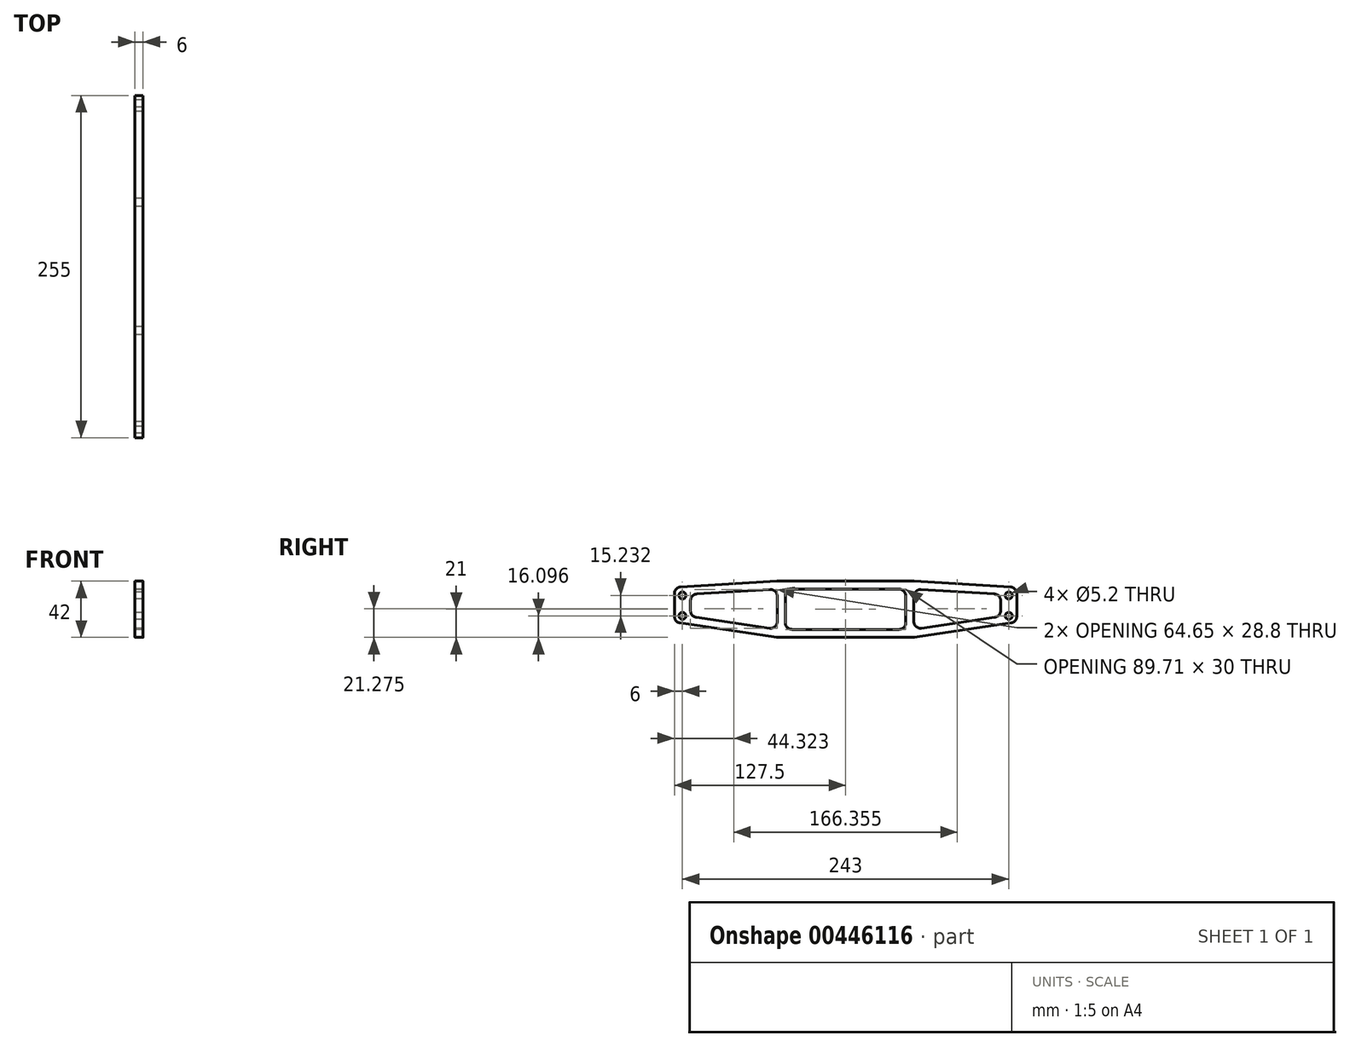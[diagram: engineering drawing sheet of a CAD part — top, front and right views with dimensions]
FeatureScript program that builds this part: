
annotation { "Feature Type Name" : "Feature", "Feature Type Description" : "" }
export const myFeature = defineFeature(function(context is Context, id is Id, definition is map)
    precondition{}
    {
        {
            var Q0;
            Q0=qCreatedBy(makeId("Right.planeOp"),FACE);
            var sketch = newSketch(context, id + "F0", { "sketchPlane" : qUnion([Q0])});
            skLineSegment(sketch, "E0.bottom", {"start": v(0, 0) * mm, "end": v(-50.48, 0) * mm});
            skLineSegment(sketch, "E0.top", {"start": v(39.16, 42) * mm, "end": v(-50.7, 42) * mm});
            skLineSegment(sketch, "E0.right", {"start": v(-50.86, 11.87) * mm, "end": v(-50.86, 30.68) * mm});
            skLineSegment(sketch, "E1", {"start": v(-127.5, 15.73) * mm, "end": v(-127.5, 32.7) * mm});
            skLineSegment(sketch, "E2", {"start": v(-122.8, 37.7) * mm, "end": v(-51, 42) * mm});
            skLineSegment(sketch, "E3", {"start": v(-123.24, 10.78) * mm, "end": v(-51.22, 0.05) * mm});
            skLineSegment(sketch, "E4.0", {"start": v(-110.8, 32.4) * mm, "end": v(-56.15, 35.67) * mm});
            skLineSegment(sketch, "E5.0", {"start": v(-111.24, 15.06) * mm, "end": v(-56.6, 6.92) * mm});
            skLineSegment(sketch, "E6.0", {"start": v(-44.86, 11) * mm, "end": v(-44.86, 31) * mm});
            skLineSegment(sketch, "E7.0", {"start": v(39.16, 36) * mm, "end": v(-39.86, 36) * mm});
            skLineSegment(sketch, "E8.0", {"start": v(0, 6) * mm, "end": v(-39.86, 6) * mm});
            skLineSegment(sketch, "E9.0", {"start": v(-115.5, 20) * mm, "end": v(-115.5, 27.42) * mm});
            skPoint(sketch, "E10.visualSharp", {"position": v(-127.5, 37.42) * mm});
            skArc(sketch, "E10.filletArc", {"start": v(-122.8, 37.7) * mm, "mid": v(-126.14, 36.14) * mm, "end": v(-127.5, 32.7) * mm});
            skPoint(sketch, "E11.visualSharp", {"position": v(-127.5, 11.42) * mm});
            skArc(sketch, "E11.filletArc", {"start": v(-127.5, 15.73) * mm, "mid": v(-126.29, 12.47) * mm, "end": v(-123.24, 10.78) * mm});
            skPoint(sketch, "E12.visualSharp", {"position": v(-115.5, 15.7) * mm});
            skArc(sketch, "E12.filletArc", {"start": v(-115.5, 20) * mm, "mid": v(-114.29, 16.74) * mm, "end": v(-111.24, 15.06) * mm});
            skPoint(sketch, "E13.visualSharp", {"position": v(-115.5, 32.13) * mm});
            skArc(sketch, "E13.filletArc", {"start": v(-110.8, 32.4) * mm, "mid": v(-114.14, 30.84) * mm, "end": v(-115.5, 27.42) * mm});
            skPoint(sketch, "E14.visualSharp", {"position": v(-50.86, 0) * mm});
            skArc(sketch, "E14.filletArc", {"start": v(-51.22, 0.05) * mm, "mid": v(-50.85, 0.01) * mm, "end": v(-50.48, 0) * mm});
            skPoint(sketch, "E15.visualSharp", {"position": v(-50.86, 42) * mm});
            skArc(sketch, "E15.filletArc", {"start": v(-50.7, 42) * mm, "mid": v(-50.85, 42) * mm, "end": v(-51, 42) * mm});
            skPoint(sketch, "E16.visualSharp", {"position": v(-44.86, 36) * mm});
            skArc(sketch, "E16.filletArc", {"start": v(-39.86, 36) * mm, "mid": v(-43.4, 34.54) * mm, "end": v(-44.86, 31) * mm});
            skPoint(sketch, "E17.visualSharp", {"position": v(-44.86, 6) * mm});
            skArc(sketch, "E17.filletArc", {"start": v(-44.86, 11) * mm, "mid": v(-43.4, 7.46) * mm, "end": v(-39.86, 6) * mm});
            skPoint(sketch, "E18.visualSharp", {"position": v(-50.86, 35.99) * mm});
            skArc(sketch, "E18.filletArc", {"start": v(-50.86, 30.68) * mm, "mid": v(-52.43, 34.32) * mm, "end": v(-56.15, 35.67) * mm});
            skPoint(sketch, "E19.visualSharp", {"position": v(-50.86, 6.07) * mm});
            skArc(sketch, "E19.filletArc", {"start": v(-56.6, 6.92) * mm, "mid": v(-52.6, 8.08) * mm, "end": v(-50.86, 11.87) * mm});
            skLineSegment(sketch, "E20", {"start": v(-115.5, 23.71) * mm, "end": v(-127.5, 23.71) * mm, "construction": true});
            skLineSegment(sketch, "E21", {"start": v(-121.5, 23.71) * mm, "end": v(-121.5, 37.78) * mm, "construction": true});
            skLineSegment(sketch, "E22", {"start": v(-121.5, 37.78) * mm, "end": v(-121.5, 10.53) * mm, "construction": true});
            skCircle(sketch, "E23", {"center": v(-121.5, 31.33) * mm, "radius": 2.6 * mm});
            skCircle(sketch, "E24.MirrorC", {"center": v(-121.5, 16.1) * mm, "radius": 2.6 * mm});
            skArc(sketch, "E25.MirrorCS", {"start": v(50.7, 42) * mm, "mid": v(50.85, 42) * mm, "end": v(51, 42) * mm});
            skArc(sketch, "E26.MirrorCS", {"start": v(51.22, 0.05) * mm, "mid": v(50.85, 0.01) * mm, "end": v(50.48, 0) * mm});
            skArc(sketch, "E27.MirrorCS", {"start": v(110.8, 32.4) * mm, "mid": v(114.14, 30.84) * mm, "end": v(115.5, 27.42) * mm});
            skArc(sketch, "E28.MirrorCS", {"start": v(39.86, 36) * mm, "mid": v(43.4, 34.54) * mm, "end": v(44.86, 31) * mm});
            skArc(sketch, "E29.MirrorCS", {"start": v(56.6, 6.92) * mm, "mid": v(52.6, 8.08) * mm, "end": v(50.86, 11.87) * mm});
            skLineSegment(sketch, "E30.MirrorCS", {"start": v(115.5, 20) * mm, "end": v(115.5, 27.42) * mm});
            skArc(sketch, "E31.MirrorCS", {"start": v(115.5, 20) * mm, "mid": v(114.29, 16.74) * mm, "end": v(111.24, 15.06) * mm});
            skArc(sketch, "E32.MirrorCS", {"start": v(50.86, 30.68) * mm, "mid": v(52.43, 34.32) * mm, "end": v(56.15, 35.67) * mm});
            skArc(sketch, "E33.MirrorCS", {"start": v(44.86, 11) * mm, "mid": v(43.4, 7.46) * mm, "end": v(39.86, 6) * mm});
            skArc(sketch, "E34.MirrorCS", {"start": v(127.5, 15.73) * mm, "mid": v(126.29, 12.47) * mm, "end": v(123.24, 10.78) * mm});
            skArc(sketch, "E35.MirrorCS", {"start": v(122.8, 37.7) * mm, "mid": v(126.14, 36.14) * mm, "end": v(127.5, 32.7) * mm});
            skPoint(sketch, "E36.MirrorP", {"position": v(44.86, 36) * mm});
            skLineSegment(sketch, "E37.MirrorCS", {"start": v(50.86, 11.87) * mm, "end": v(50.86, 30.68) * mm});
            skLineSegment(sketch, "E38.MirrorCS", {"start": v(121.5, 23.71) * mm, "end": v(121.5, 37.78) * mm, "construction": true});
            skCircle(sketch, "E39.MirrorC", {"center": v(121.5, 31.33) * mm, "radius": 2.6 * mm});
            skLineSegment(sketch, "E40.MirrorCS", {"start": v(44.86, 11) * mm, "end": v(44.86, 31) * mm});
            skPoint(sketch, "E41.MirrorP", {"position": v(127.5, 37.42) * mm});
            skPoint(sketch, "E42.MirrorP", {"position": v(50.86, 35.99) * mm});
            skLineSegment(sketch, "E43.MirrorCS", {"start": v(111.24, 15.06) * mm, "end": v(56.6, 6.92) * mm});
            skPoint(sketch, "E44.MirrorP", {"position": v(127.5, 11.42) * mm});
            skPoint(sketch, "E45.MirrorP", {"position": v(50.86, 6.07) * mm});
            skLineSegment(sketch, "E46.MirrorCS", {"start": v(123.24, 10.78) * mm, "end": v(51.22, 0.05) * mm});
            skLineSegment(sketch, "E47.MirrorCS", {"start": v(121.5, 37.78) * mm, "end": v(121.5, 10.53) * mm, "construction": true});
            skLineSegment(sketch, "E48.MirrorCS", {"start": v(110.8, 32.4) * mm, "end": v(56.15, 35.67) * mm});
            skPoint(sketch, "E49.MirrorP", {"position": v(50.86, 42) * mm});
            skCircle(sketch, "E50.MirrorC", {"center": v(121.5, 16.1) * mm, "radius": 2.6 * mm});
            skLineSegment(sketch, "E51.MirrorCS", {"start": v(115.5, 23.71) * mm, "end": v(127.5, 23.71) * mm, "construction": true});
            skLineSegment(sketch, "E52.MirrorCS", {"start": v(122.8, 37.7) * mm, "end": v(51, 42) * mm});
            skLineSegment(sketch, "E53.MirrorCS", {"start": v(127.5, 15.73) * mm, "end": v(127.5, 32.7) * mm});
            skPoint(sketch, "E54.MirrorP", {"position": v(50.86, 0) * mm});
            skPoint(sketch, "E55.MirrorP", {"position": v(44.86, 6) * mm});
            skPoint(sketch, "E56.MirrorP", {"position": v(115.5, 15.7) * mm});
            skPoint(sketch, "E57.MirrorP", {"position": v(115.5, 32.13) * mm});
            skLineSegment(sketch, "E58.MirrorCS", {"start": v(-39.16, 36) * mm, "end": v(39.86, 36) * mm});
            skLineSegment(sketch, "E59.MirrorCS", {"start": v(-39.16, 42) * mm, "end": v(50.7, 42) * mm});
            skLineSegment(sketch, "E60.MirrorCS", {"start": v(0, 6) * mm, "end": v(39.86, 6) * mm});
            skLineSegment(sketch, "E61.MirrorCS", {"start": v(0, 0) * mm, "end": v(50.48, 0) * mm});
            skSolve(sketch);
        }
        {
            var Q0;
            Q0=makeQuery(id+"F0.imprint","IMPRINT",FACE,{"disambiguationData":[TD([[makeQuery(id+"F0.imprint","IMPRINT",EDGE,{"derivedFrom":sQuery(id+"F0.wireOp",EDGE,"E0.bottom")}),-1.0]])]});
            extrude(context, id + "F1", {"entities" : qUnion([Q0]), "depth" : 6 * mm});
        }
    });
